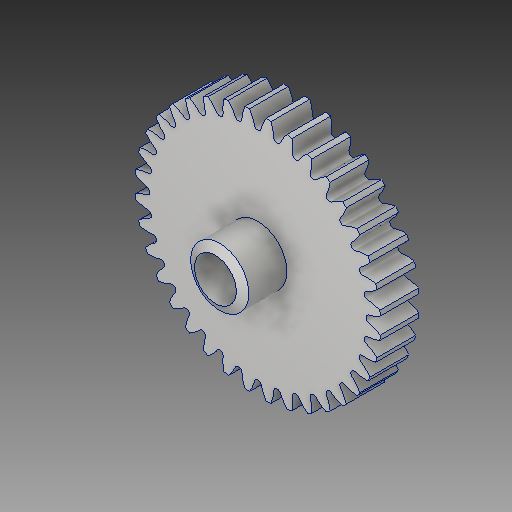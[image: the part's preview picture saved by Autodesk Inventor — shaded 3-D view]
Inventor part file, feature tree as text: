
AUTODESK INVENTOR PART (.ipt)
format: ipt  version: 2017 (Build 210142000, 142)  size: 407,552 bytes
history: native  units: in
note: dims shown in document units (in); Inventor stores cm internally (conversion verified against a paired STEP export)
features: chamfer x1
ambient origin geometry x8: Origin, YZ Plane, XZ Plane, XY Plane, X Axis, Y Axis, Z Axis, Center Point
bodies: Solid1 (feature_tree)
feature tree (1):
  chamfer  "Chamfer1"  [1 undecoded]
note: 1 required parameter value undecoded (feature->parameter linkage not recoverable at this tier; creation-order binding heuristic only, values carry confidence <= 0.55)
